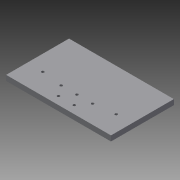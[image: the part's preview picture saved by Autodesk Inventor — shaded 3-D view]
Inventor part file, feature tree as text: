
AUTODESK INVENTOR PART (.ipt)
format: ipt  version: 2013 (Build 170138000, 138)  size: 96,256 bytes
history: native  units: in
note: dims shown in document units (in); Inventor stores cm internally (conversion verified against a paired STEP export)
features: sketch x3, hole x2, extrude x1
ambient origin geometry x8: Origin, YZ Plane, XZ Plane, XY Plane, X Axis, Y Axis, Z Axis, Center Point
bodies: Solid1 (feature_tree)
feature tree (6):
  extrude  "Extrusion1"  Depth=6.0in
  hole  "Hole1"  [1 undecoded]
  hole  "Hole5"  [1 undecoded]
  sketch  "Sketch1"  dims[d0=10.0in d1=6.0in]
  sketch  "Sketch5"  dims[d2=0.5in d3=0.0in d20=2.0in]
  sketch  "Sketch10"  dims[d21=1.5in d22=1.5in d23=0.25in d24=0.75in d25=0.375in d26=0.25in d27=0.5635in d28=1.0in d29=0.8108in d67=1.5in d69=1.5in d70=0.75in d71=0.75in d72=5.0in d73=5.0in d74=0.75in d75=1.0in d76=0.25in d77=0.75in d78=0.375in d79=0.25in d80=0.5635in d81=1.0in d82=0.8108in]
note: 2 required parameter values undecoded (feature->parameter linkage not recoverable at this tier; creation-order binding heuristic only, values carry confidence <= 0.55)
